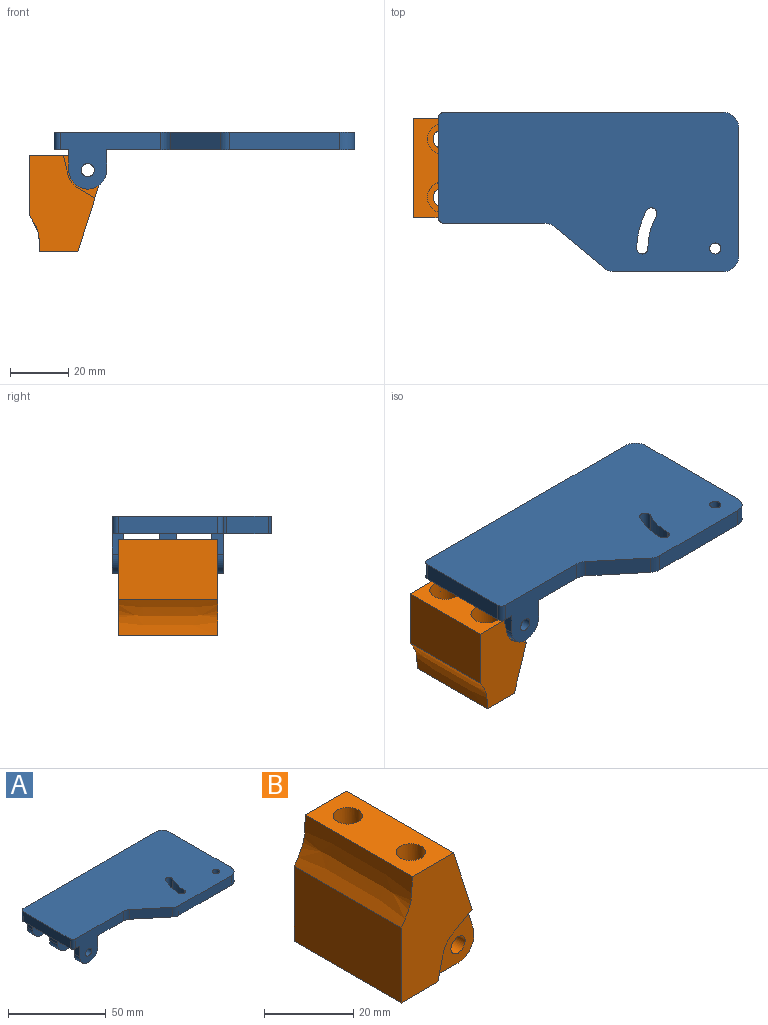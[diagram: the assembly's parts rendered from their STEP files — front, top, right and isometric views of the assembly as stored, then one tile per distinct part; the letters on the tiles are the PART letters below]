
ASSEMBLY  parts=2 mates=1
PART A: 35 faces, bbox 103x54.6x19.5 mm
  f0: plane 34.56x19.5mm, normal (0,-1,0), area 348.8mm2, adj f4,f12,f13,f24,f25,f27,f31,f32
  f1: plane 13.5x13mm, normal (0,-1,0), area 141.5mm2, adj f2,f25,f26,f33,f34
  f2: plane 7x5.9mm, normal (-1,0,0), area 41.3mm2, adj f1,f3,f25,f33
  f3: plane 13.5x13mm, normal (0,1,0), area 141.5mm2, adj f2,f25,f26,f33,f34
  f4: plane 7x3.9mm, normal (-1,0,0), area 27.3mm2, adj f0,f5,f25,f31
  f5: plane 13.5x13mm, normal (0,1,0), area 141.5mm2, adj f4,f25,f27,f31,f32
  f6: plane 7x3.8mm, normal (-1,0,0), area 26.6mm2, adj f7,f9,f25,f30
  f7: plane 13.5x13mm, normal (0,-1,0), area 141.5mm2, adj f6,f25,f28,f29,f30
  f8: cylinder r=5mm len=6mm, axis (0,0,-1), area 47.1mm2, adj f9,f23,f24,f25
  f9: plane 96.01x19.5mm, normal (0,1,0), area 717.5mm2, adj f6,f8,f10,f24,f25,f28,f29,f30
  f10: cylinder r=2mm len=6mm, axis (0,0,-1), area 18.8mm2, adj f9,f11,f24,f25
  f11: plane 34x6mm, normal (-1,0,0), area 204mm2, adj f10,f12,f24,f25
  f12: cylinder r=2mm len=6mm, axis (0,0,-1), area 18.8mm2, adj f0,f11,f24,f25
  f13: cylinder r=5mm len=6mm, axis (0,0,-1), area 20.7mm2, adj f0,f14,f24,f25
  f14: plane 17.25x14.28mm, normal (-0.64,-0.77,0), area 134.3mm2, adj f13,f15,f24,f25
  f15: cylinder r=5mm len=6mm, axis (0,0,-1), area 20.7mm2, adj f14,f16,f24,f25
  f16: plane 37.83x6mm, normal (0,-1,0), area 227mm2, adj f15,f17,f24,f25
  f17: cylinder r=5mm len=6mm, axis (0,0,-1), area 47.1mm2, adj f16,f23,f24,f25
  f18: cylinder r=1.9mm len=6mm, axis (0,0,-1), area 35.8mm2, adj f19,f22,f24,f25
  f19: cylinder r=26.9mm len=12.97mm, axis (0,0,-1), area 81.2mm2, adj f18,f20,f24,f25
  f20: cylinder r=1.9mm len=6mm, axis (0,0,-1), area 35.8mm2, adj f19,f22,f24,f25
  f21: cylinder r=1.9mm len=6mm, axis (0,0,-1), area 71.6mm2, adj f24,f25
  f22: cylinder r=23.1mm len=11.14mm, axis (0,0,-1), area 69.7mm2, adj f18,f20,f24,f25
  f23: plane 44.57x6mm, normal (1,0,0), area 267.4mm2, adj f8,f17,f24,f25
  f24: plane 103.01x54.57mm, normal (0,0,1), area 4737mm2, adj f0,f8,f9,f10,f11,f12,f13,f14
  f25: plane 103.01x54.57mm, normal (0,0,-1), area 4560.2mm2, adj f0,f1,f2,f3,f4,f5,f6,f7
  f26: plane 7x5.9mm, normal (1,0,0), area 41.3mm2, adj f1,f3,f25,f33
  f27: plane 7x3.9mm, normal (1,0,0), area 27.3mm2, adj f0,f5,f25,f31
  f28: plane 7x3.8mm, normal (1,0,0), area 26.6mm2, adj f7,f9,f25,f30
  f29: cylinder r=2.25mm len=4.5mm, axis (0,1,0), area 53.7mm2, adj f7,f9
  f30: cylinder r=6.5mm len=13mm, axis (0,1,0), area 77.6mm2, adj f6,f7,f9,f28
  f31: cylinder r=6.5mm len=13mm, axis (0,1,0), area 79.6mm2, adj f0,f4,f5,f27
  f32: cylinder r=2.25mm len=4.5mm, axis (0,1,0), area 55.1mm2, adj f0,f5
  f33: cylinder r=6.5mm len=13mm, axis (0,1,0), area 120.5mm2, adj f1,f2,f3,f26
  f34: cylinder r=2.25mm len=5.9mm, axis (0,1,0), area 83.4mm2, adj f1,f3
PART B: 32 faces, bbox 25x34x33 mm
  f0: plane 12x1.55mm, normal (1,0,0), area 18.6mm2, adj f1,f4,f23,f27
  f1: plane 34x26.45mm, normal (0.95,0,0.3), area 859.6mm2, adj f0,f5,f7,f11,f12,f18,f19,f23
  f2: cylinder r=2.25mm len=12mm, axis (0,-1,0), area 169.6mm2, adj f23,f27
  f3: plane 34x20mm, normal (0,0,-1), area 423mm2, adj f4,f7,f10,f11,f14,f16,f18,f21
  f4: cylinder r=5mm len=12mm, axis (0,1,0), area 94.2mm2, adj f0,f3,f23,f27
  f5: plane 12x1.55mm, normal (1,0,0), area 18.6mm2, adj f1,f18,f26,f28
  f6: cylinder r=2.25mm len=12mm, axis (0,-1,0), area 169.6mm2, adj f18,f28
  f7: plane 33x22.46mm, normal (0,1,0), area 542.3mm2, adj f1,f3,f10,f12,f13,f22,f24,f25
  f8: cylinder r=3.25mm len=8mm, axis (0,0,-1), area 163.4mm2, adj f12,f17
  f9: cylinder r=3.25mm len=8mm, axis (0,0,-1), area 163.4mm2, adj f12,f15
  f10: plane 34x20.6mm, normal (-1,0,0), area 700.5mm2, adj f3,f7,f11,f13
  f11: plane 33x22.46mm, normal (0,-1,0), area 542.2mm2, adj f1,f3,f10,f12,f13,f19,f20,f21
  f12: plane 34x13.14mm, normal (0,0,1), area 380.5mm2, adj f1,f7,f8,f9,f11,f13
  f13: extruded ~34x12.4mm, area 448.5mm2, adj f7,f10,f11,f12
  f14: cylinder r=5.25mm len=25mm, axis (0,0,-1), area 824.7mm2, adj f3,f15
  f15: plane 10.5x10.5mm, normal (0,0,-1), area 53.4mm2, adj f9,f14
  f16: cylinder r=5.25mm len=25mm, axis (0,0,-1), area 824.7mm2, adj f3,f17
  f17: plane 10.5x10.5mm, normal (0,0,-1), area 53.4mm2, adj f8,f16
  f18: plane 14.55x13.38mm, normal (0,-1,0), area 118.5mm2, adj f1,f3,f5,f6,f19,f20,f21,f26
  f19: plane 6x3.51mm, normal (0.51,0,-0.86), area 13.9mm2, adj f1,f11,f18,f20
  f20: cylinder r=7mm len=4.44mm, axis (0,-1,0), area 11.3mm2, adj f11,f18,f19,f21
  f21: plane 6.6x2mm, normal (0.97,0,-0.23), area 13.6mm2, adj f3,f11,f18,f20
  f22: plane 7.08x2mm, normal (0.97,0,-0.24), area 14.6mm2, adj f3,f7,f23,f24
  f23: plane 14.55x13.39mm, normal (0,1,0), area 118.3mm2, adj f0,f1,f2,f3,f4,f22,f24,f25
  f24: cylinder r=6.99mm len=3.97mm, axis (0,1,0), area 10.4mm2, adj f7,f22,f23,f25
  f25: plane 5.97x3.5mm, normal (0.51,0,-0.86), area 13.8mm2, adj f1,f7,f23,f24
  f26: cylinder r=5mm len=12mm, axis (0,1,0), area 94.2mm2, adj f3,f5,f18,f28
  f27: plane 14.55x13.38mm, normal (0,-1,0), area 118.5mm2, adj f0,f1,f2,f3,f4,f29,f30,f31
  f28: plane 14.55x13.38mm, normal (0,1,0), area 118.5mm2, adj f1,f3,f5,f6,f26,f29,f30,f31
  f29: plane 6x6mm, normal (0.51,0,-0.86), area 41.7mm2, adj f1,f27,f28,f30
  f30: cylinder r=7mm len=6mm, axis (0,-1,0), area 34mm2, adj f27,f28,f29,f31
  f31: plane 6.6x6mm, normal (0.97,0,-0.23), area 40.7mm2, adj f3,f27,f28,f30
PLACE A t=(94.21,-25.89,-10.94)mm
PLACE B rot(axis=(1,0,0),180deg) t=(18.52,-15.04,-12.94)mm
MATE cylindrical B.f2 <-> A.f29  axis (0,-1,0) through (28.52,-31.04,-17.94)mm
